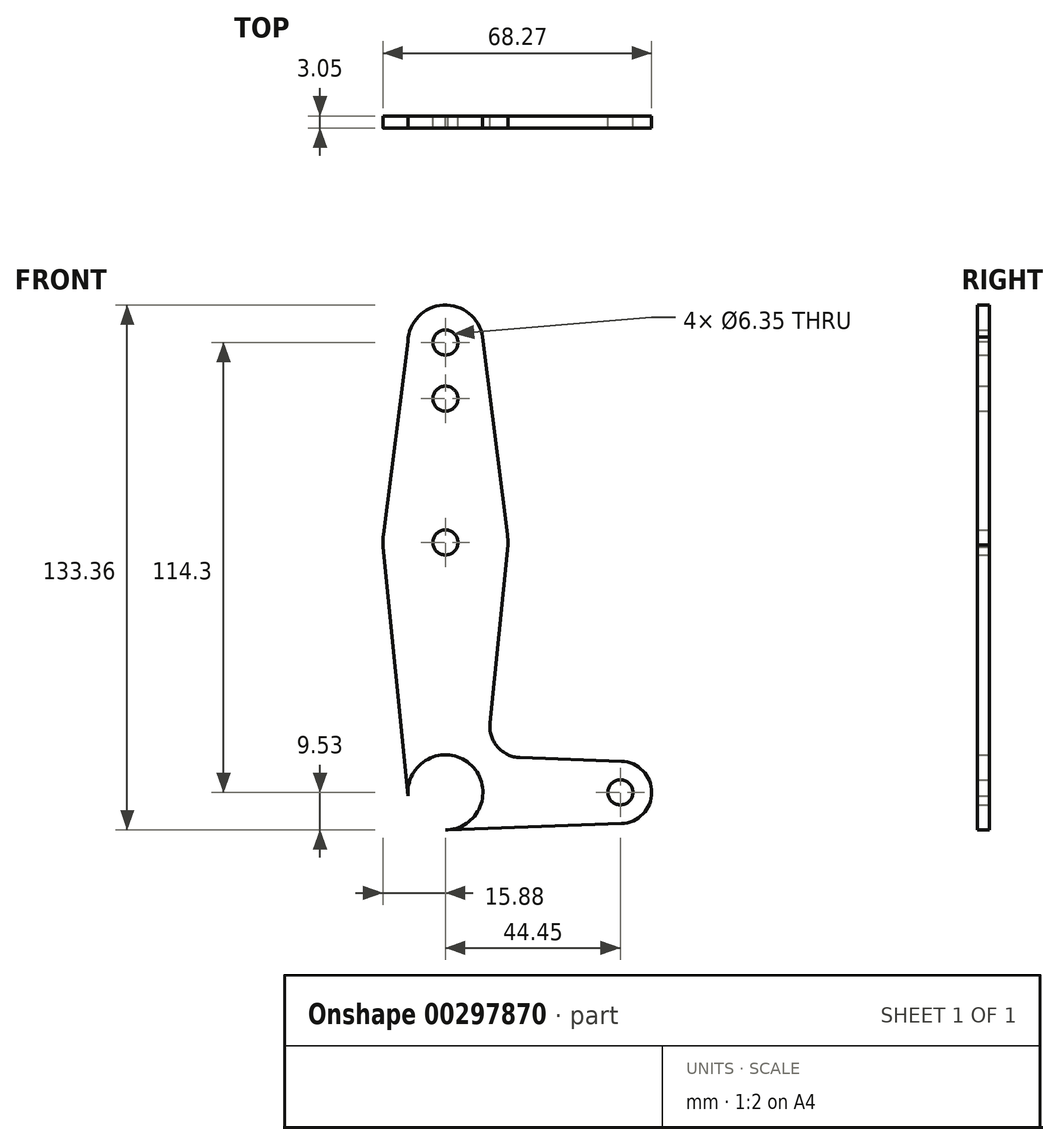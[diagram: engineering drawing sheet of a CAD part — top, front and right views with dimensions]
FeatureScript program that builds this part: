
annotation { "Feature Type Name" : "Feature", "Feature Type Description" : "" }
export const myFeature = defineFeature(function(context is Context, id is Id, definition is map)
    precondition{}
    {
        {
            var Q0;
            Q0=qCreatedBy(makeId("Front.planeOp"),FACE);
            var sketch = newSketch(context, id + "F0", { "sketchPlane" : qUnion([Q0])});
            skLineSegment(sketch, "E0", {"start": v(0, 0) * mm, "end": v(0, 114.3) * mm, "construction": true});
            skLineSegment(sketch, "E1", {"start": v(0, 0) * mm, "end": v(44.45, 0) * mm, "construction": true});
            skCircle(sketch, "E2", {"center": v(0, 114.3) * mm, "radius": 9.53 * mm});
            skCircle(sketch, "E3", {"center": v(0, 63.5) * mm, "radius": 15.88 * mm});
            skCircle(sketch, "E4", {"center": v(0, 0) * mm, "radius": 9.53 * mm});
            skCircle(sketch, "E5", {"center": v(44.45, 0) * mm, "radius": 7.94 * mm});
            skLineSegment(sketch, "E6", {"start": v(9.42, 115.7) * mm, "end": v(15.75, 65.49) * mm});
            skLineSegment(sketch, "E7", {"start": v(-9.52, 114.6) * mm, "end": v(-15.75, 65.5) * mm});
            skLineSegment(sketch, "E8", {"start": v(15.86, 62.88) * mm, "end": v(11.33, 17.59) * mm});
            skLineSegment(sketch, "E9", {"start": v(18.96, 8.85) * mm, "end": v(44.73, 7.93) * mm});
            skLineSegment(sketch, "E10", {"start": v(0, -9.53) * mm, "end": v(44.73, -7.93) * mm});
            skCircle(sketch, "E11", {"center": v(0, 114.3) * mm, "radius": 3.18 * mm});
            skCircle(sketch, "E12", {"center": v(0, 63.5) * mm, "radius": 3.18 * mm});
            skLineSegment(sketch, "E13", {"start": v(-15.83, 62.36) * mm, "end": v(-9.48, -0.95) * mm});
            skPoint(sketch, "E14.newPointB", {"position": v(0, 9.53) * mm});
            skArc(sketch, "E14.filletArc", {"start": v(11.33, 17.59) * mm, "mid": v(13.25, 11.57) * mm, "end": v(18.96, 8.85) * mm});
            skCircle(sketch, "E15", {"center": v(0, 0) * mm, "radius": 3.18 * mm});
            skCircle(sketch, "E16", {"center": v(44.45, 0) * mm, "radius": 3.18 * mm});
            skCircle(sketch, "E17", {"center": v(0, 100.03) * mm, "radius": 3.18 * mm});
            skSolve(sketch);
        }
        {
            var Q0;
            Q0=makeQuery(id+"F0.imprint","IMPRINT",FACE,{"disambiguationData":[TD([[makeQuery(id+"F0.imprint","IMPRINT",EDGE,{"derivedFrom":sQuery(id+"F0.wireOp",EDGE,"E11")}),-1.0]])]});
            var Q1;
            Q1=makeQuery(id+"F0.imprint","IMPRINT",FACE,{"disambiguationData":[TD([[makeQuery(id+"F0.imprint","IMPRINT",EDGE,{"derivedFrom":sQuery(id+"F0.wireOp",EDGE,"E12")}),-1.0]])]});
            var Q2;
            {var subQ0=sQuery(id+"F0.wireOp",EDGE,"E7");Q2=makeQuery(id+"F0.imprint","IMPRINT",FACE,{"disambiguationData":[TD([[makeQuery(id+"F0.imprint","IMPRINT",EDGE,{"derivedFrom":subQ0}),1.0]])]});}
            var Q3;
            {var subQ4=sQuery(id+"F0.wireOp",EDGE,"E9");Q3=makeQuery(id+"F0.imprint","IMPRINT",FACE,{"disambiguationData":[TD([[makeQuery(id+"F0.imprint","IMPRINT",EDGE,{"derivedFrom":subQ4}),-1.0]])]});}
            var Q4;
            {var subQ0=sQuery(id+"F0.wireOp",EDGE,"E10");var subQ1=sQuery(id+"F0.wireOp",EDGE,"E4");var subQ2=makeQuery(id+"F0.imprint","INTERSECT",VERTEX,{"disambiguationData":[OD(0.0)],"derivedFrom":[subQ1,subQ0]});Q4=makeQuery(id+"F0.imprint","IMPRINT",FACE,{"disambiguationData":[TD([[makeQuery(id+"F0.imprint","IMPRINT",EDGE,{"disambiguationData":[TD([[subQ2,1.0]])],"derivedFrom":subQ1}),1.0]])]});}
            var Q5;
            {var subQ0=sQuery(id+"F0.wireOp",EDGE,"E5");var subQ1=makeQuery(id+"F0.imprint","INTERSECT",VERTEX,{"derivedFrom":[subQ0,sQuery(id+"F0.wireOp",EDGE,"E9")]});Q5=makeQuery(id+"F0.imprint","IMPRINT",FACE,{"disambiguationData":[TD([[makeQuery(id+"F0.imprint","IMPRINT",EDGE,{"disambiguationData":[TD([[subQ1,-1.0]])],"derivedFrom":subQ0}),1.0]])]});}
            extrude(context, id + "F1", {"entities" : qUnion([Q0, Q1, Q2, Q3, Q4, Q5]), "depth" : 3.05 * mm});
        }
    });
